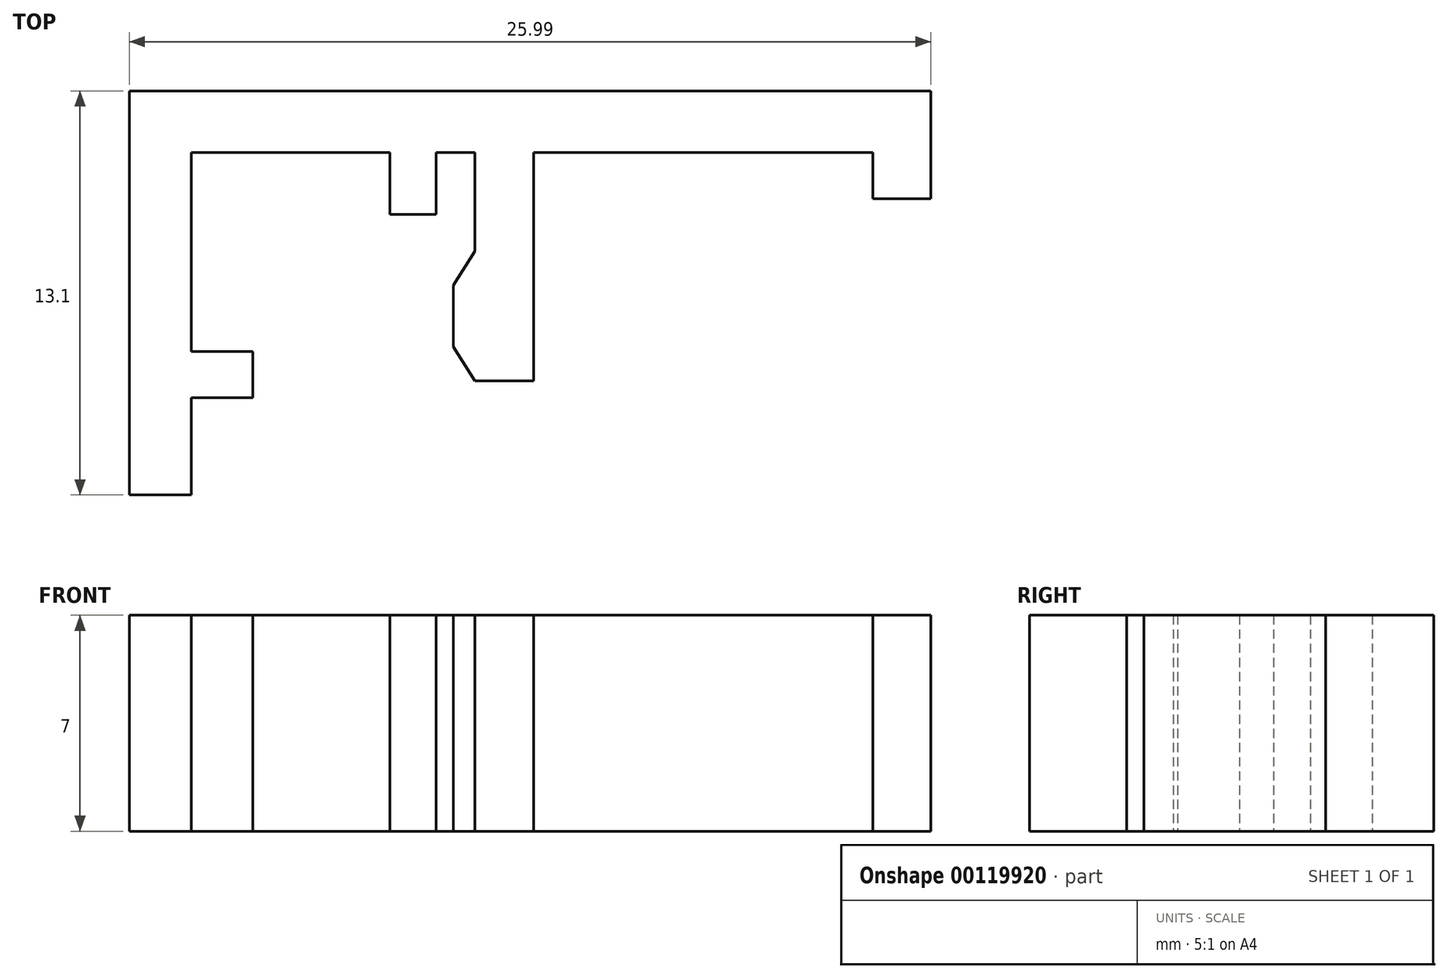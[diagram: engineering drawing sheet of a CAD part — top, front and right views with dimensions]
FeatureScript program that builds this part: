
annotation { "Feature Type Name" : "Feature", "Feature Type Description" : "" }
export const myFeature = defineFeature(function(context is Context, id is Id, definition is map)
    precondition{}
    {
        {
            var Q0;
            Q0=qCreatedBy(makeId("Top.planeOp"),FACE);
            var sketch = newSketch(context, id + "F0", { "sketchPlane" : qUnion([Q0])});
            skLineSegment(sketch, "E0.bottom", {"start": v(-0.9, 0) * mm, "end": v(-2.8, 0) * mm});
            skLineSegment(sketch, "E0.top", {"start": v(-0.9, -7.4) * mm, "end": v(-2.8, -7.4) * mm});
            skLineSegment(sketch, "E0.left", {"start": v(-0.9, 0) * mm, "end": v(-0.9, -7.4) * mm});
            skLineSegment(sketch, "E0.right", {"start": v(-2.8, 0) * mm, "end": v(-2.8, -7.4) * mm});
            skLineSegment(sketch, "E1", {"start": v(-2.8, -7.4) * mm, "end": v(-3.5, -6.3) * mm});
            skLineSegment(sketch, "E2", {"start": v(-3.5, -6.3) * mm, "end": v(-3.5, -4.3) * mm});
            skLineSegment(sketch, "E3", {"start": v(-3.5, -4.3) * mm, "end": v(-2.8, -3.2) * mm});
            skLineSegment(sketch, "E4", {"start": v(-2.8, 0) * mm, "end": v(-4.05, 0) * mm});
            skLineSegment(sketch, "E5", {"start": v(-4.05, 0) * mm, "end": v(-4.05, -2) * mm});
            skLineSegment(sketch, "E6", {"start": v(-4.05, -2) * mm, "end": v(-5.55, -2) * mm});
            skLineSegment(sketch, "E7", {"start": v(-5.55, -2) * mm, "end": v(-5.55, 2) * mm});
            skLineSegment(sketch, "E8", {"start": v(-5.55, 2) * mm, "end": v(0, 2) * mm});
            skLineSegment(sketch, "E9", {"start": v(-10, -2) * mm, "end": v(0, -12) * mm, "construction": true});
            skLineSegment(sketch, "E10", {"start": v(-5.55, -2) * mm, "end": v(-18.54, -2) * mm, "construction": true});
            skLineSegment(sketch, "E11.MirrorCS", {"start": v(-10, -7.95) * mm, "end": v(-10, -6.45) * mm});
            skLineSegment(sketch, "E12.MirrorCS", {"start": v(-10, -6.45) * mm, "end": v(-14, -6.45) * mm});
            skLineSegment(sketch, "E13.MirrorCS", {"start": v(-12, -7.95) * mm, "end": v(-10, -7.95) * mm});
            skLineSegment(sketch, "E14.MirrorCS", {"start": v(-14, -6.45) * mm, "end": v(-14, -11.1) * mm});
            skLineSegment(sketch, "E15.MirrorCS", {"start": v(-12, -9.2) * mm, "end": v(-12, -7.95) * mm});
            skLineSegment(sketch, "E16.MirrorCS", {"start": v(-12, -11.1) * mm, "end": v(-12, -9.2) * mm});
            skLineSegment(sketch, "E17", {"start": v(-12, -6.45) * mm, "end": v(-12, 0) * mm});
            skLineSegment(sketch, "E18", {"start": v(-12, 0) * mm, "end": v(-5.55, 0) * mm});
            skLineSegment(sketch, "E19", {"start": v(-14, -6.45) * mm, "end": v(-14, 2) * mm});
            skLineSegment(sketch, "E20", {"start": v(-14, 2) * mm, "end": v(-5.55, 2) * mm});
            skLineSegment(sketch, "E21", {"start": v(-12, -11.1) * mm, "end": v(-14, -11.1) * mm});
            skLineSegment(sketch, "E22", {"start": v(-0.9, 0) * mm, "end": v(10.1, 0) * mm});
            skLineSegment(sketch, "E23", {"start": v(10.1, 0) * mm, "end": v(10.1, -1.5) * mm});
            skLineSegment(sketch, "E24", {"start": v(10.1, -1.5) * mm, "end": v(11.99, -1.5) * mm});
            skLineSegment(sketch, "E25", {"start": v(11.99, -1.5) * mm, "end": v(11.99, 2) * mm});
            skLineSegment(sketch, "E26", {"start": v(11.99, 2) * mm, "end": v(0, 2) * mm});
            skLineSegment(sketch, "E27", {"start": v(0, -12) * mm, "end": v(-18.74, -12) * mm, "construction": true});
            skSolve(sketch);
        }
        {
            var Q0;
            Q0=qSketchRegion(id+"F0",true);
            extrude(context, id + "F1", {"entities" : qUnion([Q0]), "depth" : 7 * mm});
        }
    });
